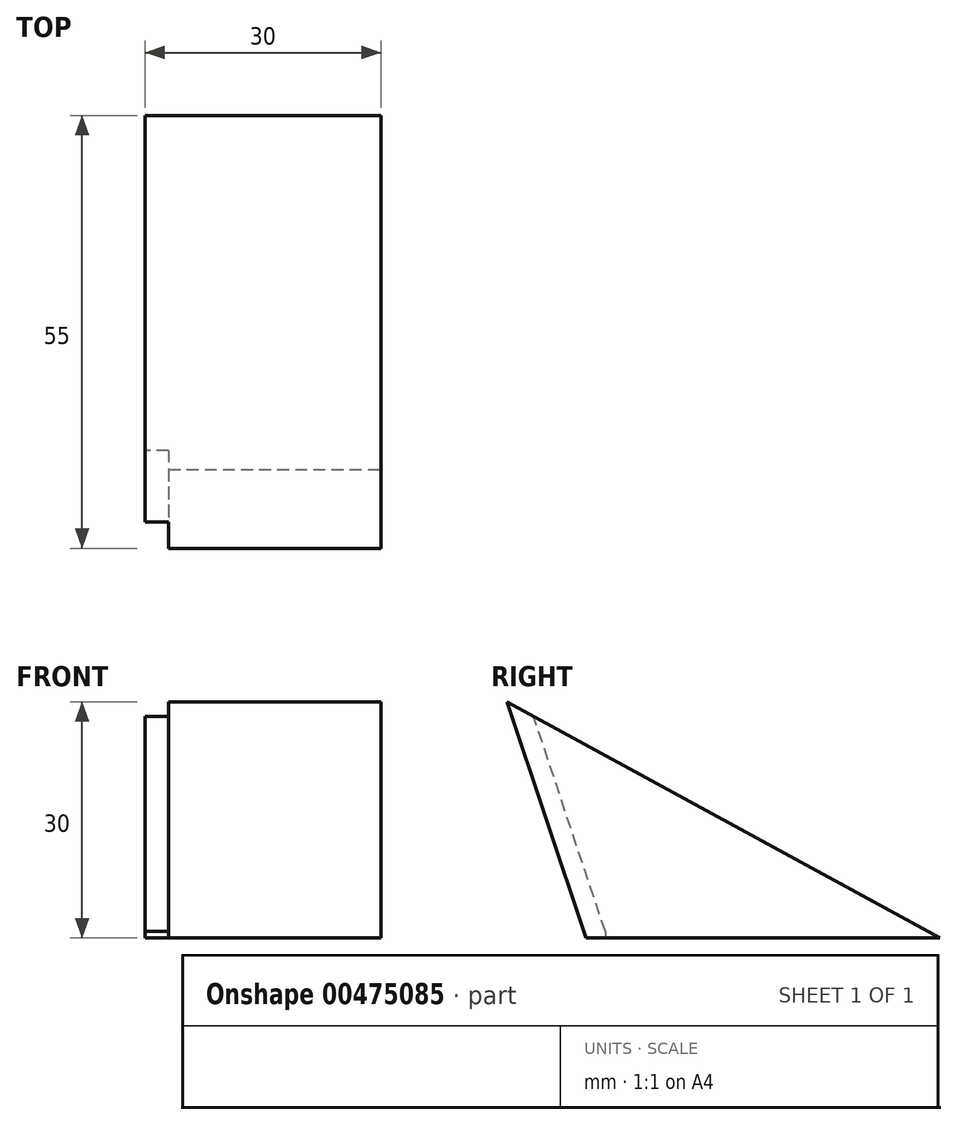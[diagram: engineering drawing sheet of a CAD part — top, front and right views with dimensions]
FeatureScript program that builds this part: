
annotation { "Feature Type Name" : "Feature", "Feature Type Description" : "" }
export const myFeature = defineFeature(function(context is Context, id is Id, definition is map)
    precondition{}
    {
        {
            var Q0;
            Q0=qCreatedBy(makeId("Top.planeOp"),FACE);
            var sketch = newSketch(context, id + "F0", { "sketchPlane" : qUnion([Q0])});
            skLineSegment(sketch, "E0.bottom", {"start": v(-15, 22.5) * mm, "end": v(15, 22.5) * mm});
            skLineSegment(sketch, "E0.top", {"start": v(-15, -22.5) * mm, "end": v(15, -22.5) * mm});
            skLineSegment(sketch, "E0.left", {"start": v(-15, 22.5) * mm, "end": v(-15, -22.5) * mm});
            skLineSegment(sketch, "E0.right", {"start": v(15, 22.5) * mm, "end": v(15, -22.5) * mm});
            skPoint(sketch, "E0.middle", {"position": v(0, 0) * mm});
            skLineSegment(sketch, "E1", {"start": v(15, -22.5) * mm, "end": v(15, -32.5) * mm});
            skLineSegment(sketch, "E2", {"start": v(15, -32.5) * mm, "end": v(-15, -32.5) * mm});
            skLineSegment(sketch, "E3", {"start": v(-15, -32.5) * mm, "end": v(-15, -22.5) * mm});
            skLineSegment(sketch, "E4", {"start": v(-15, -22.5) * mm, "end": v(-15, -19.5) * mm});
            skSolve(sketch);
        }
        {
            var Q0;
            Q0=makeQuery(id+"F0.imprint","IMPRINT",FACE,{"disambiguationData":[TD([[makeQuery(id+"F0.imprint","IMPRINT",EDGE,{"derivedFrom":sQuery(id+"F0.wireOp",EDGE,"E0.bottom")}),-1.0]])]});
            var Q1;
            Q1=makeQuery(id+"F0.imprint","IMPRINT",FACE,{"disambiguationData":[TD([[makeQuery(id+"F0.imprint","IMPRINT",EDGE,{"derivedFrom":sQuery(id+"F0.wireOp",EDGE,"E0.top")}),-1.0]])]});
            extrude(context, id + "F1", {"entities" : qUnion([Q0, Q1]), "depth" : 30 * mm});
        }
        {
            var Q0;
            Q0=makeQuery(id+"F1.opExtrude","SWEPT_FACE",FACE,{"disambiguationData":[OSD([sQuery(id+"F0.wireOp",EDGE,"E0.right"),sQuery(id+"F0.wireOp",EDGE,"E1")])]});
            var sketch = newSketch(context, id + "F2", { "sketchPlane" : qUnion([Q0])});
            skLineSegment(sketch, "E5.0", {"start": v(-22.5, 0) * mm, "end": v(-32.5, 0) * mm});
            skLineSegment(sketch, "E6", {"start": v(-22.5, 0) * mm, "end": v(-32.5, 30) * mm});
            skLineSegment(sketch, "E7", {"start": v(-32.5, 30) * mm, "end": v(22.5, 0) * mm});
            skLineSegment(sketch, "E8", {"start": v(0, 0) * mm, "end": v(-5, 0) * mm});
            skLineSegment(sketch, "E9", {"start": v(0, 0) * mm, "end": v(5, 0) * mm});
            skLineSegment(sketch, "E10", {"start": v(-5, 0) * mm, "end": v(-5, 6) * mm});
            skLineSegment(sketch, "E11", {"start": v(-5, 6) * mm, "end": v(5, 6) * mm});
            skLineSegment(sketch, "E12", {"start": v(5, 6) * mm, "end": v(5, 0) * mm});
            skSolve(sketch);
        }
        {
            var Q0;
            Q0=makeQuery(id+"F2.imprint","IMPRINT",FACE,{"disambiguationData":[TD([[makeQuery(id+"F2.imprint","IMPRINT",EDGE,{"derivedFrom":sQuery(id+"F2.wireOp",EDGE,"E5.0")}),-1.0]])]});
            var Q1;
            Q1=makeQuery(id+"F2.imprint","IMPRINT",FACE,{"disambiguationData":[TD([[makeQuery(id+"F2.imprint","IMPRINT",EDGE,{"derivedFrom":sQuery(id+"F2.wireOp",EDGE,"E7")}),1.0]])]});
            extrude(context, id + "F3", {"entities" : qUnion([Q0, Q1]), "operationType" : NewBodyOperationType.REMOVE, "endBound" : BoundingType.THROUGH_ALL, "oppositeDirection" : true, "depth" : 25 * mm});
        }
        {
            var Q0;
            Q0=makeQuery(id+"F3.boolean.opBoolean","COPY",FACE,{"derivedFrom":makeQuery(id+"F3.opExtrude","SWEPT_FACE",FACE,{"disambiguationData":[OSD([sQuery(id+"F2.wireOp",EDGE,"E6")])]})});
            var sketch = newSketch(context, id + "F4", { "sketchPlane" : qUnion([Q0])});
            skLineSegment(sketch, "E13", {"start": v(-15, 7.12) * mm, "end": v(-12, 7.12) * mm});
            skLineSegment(sketch, "E14", {"start": v(-12, 7.12) * mm, "end": v(-12, 38.74) * mm});
            skSolve(sketch);
        }
        {
            var Q0;
            Q0=makeQuery(id+"F4.imprint","IMPRINT",FACE,{"disambiguationData":[TD([[makeQuery(id+"F4.imprint","IMPRINT",EDGE,{"derivedFrom":sQuery(id+"F4.wireOp",EDGE,"E13")}),1.0]])]});
            extrude(context, id + "F5", {"entities" : qUnion([Q0]), "operationType" : NewBodyOperationType.REMOVE, "oppositeDirection" : true, "depth" : 2.6 * mm});
        }
        {
            var Q0;
            Q0=makeQuery(id+"F1.opExtrude","SWEPT_FACE",FACE,{"disambiguationData":[OSD([sQuery(id+"F0.wireOp",EDGE,"E0.left"),sQuery(id+"F0.wireOp",EDGE,"E3"),sQuery(id+"F0.wireOp",EDGE,"E4")])]});
            var sketch = newSketch(context, id + "F6", { "sketchPlane" : qUnion([Q0])});
            skLineSegment(sketch, "E15", {"start": v(20.03, 0.82) * mm, "end": v(20.03, 0) * mm});
            skSolve(sketch);
        }
        {
            var Q0;
            {var subQ0=sQuery(id+"F6.wireOp",EDGE,"E15");Q0=makeQuery(id+"F6.imprint","IMPRINT",FACE,{"disambiguationData":[TD([[makeQuery(id+"F6.imprint","IMPRINT",EDGE,{"derivedFrom":subQ0}),1.0]])]});}
            extrude(context, id + "F7", {"entities" : qUnion([Q0]), "operationType" : NewBodyOperationType.REMOVE, "oppositeDirection" : true, "depth" : 3 * mm});
        }
    });
